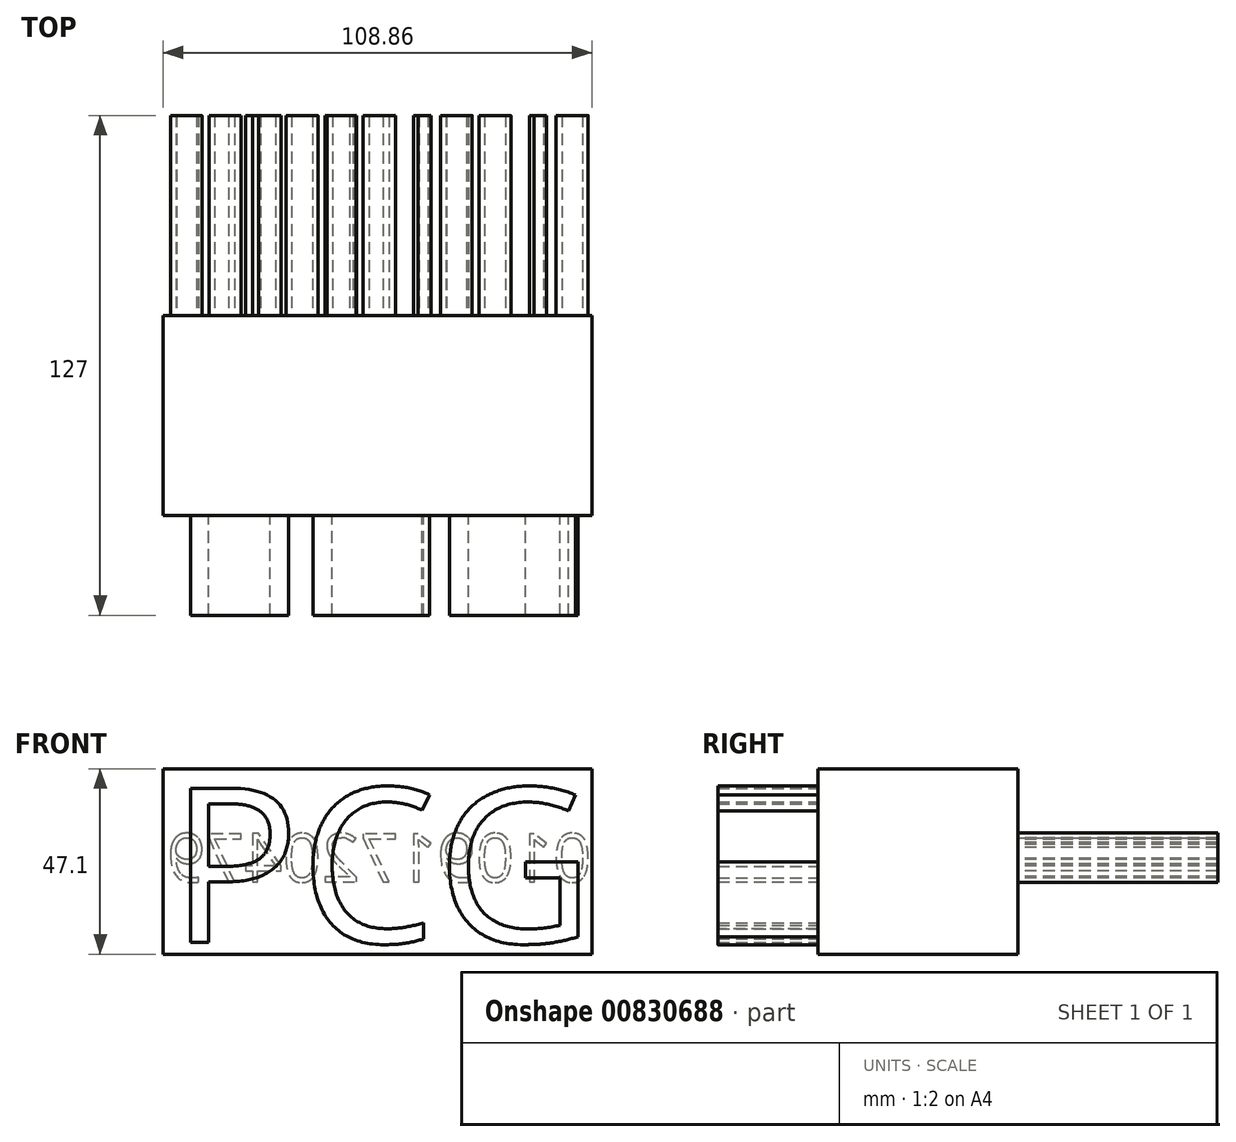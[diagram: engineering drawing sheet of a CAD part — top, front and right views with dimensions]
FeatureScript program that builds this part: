
annotation { "Feature Type Name" : "Feature", "Feature Type Description" : "" }
export const myFeature = defineFeature(function(context is Context, id is Id, definition is map)
    precondition{}
    {
        {
            var Q0;
            Q0=qCreatedBy(makeId("Front.planeOp"),FACE);
            var sketch = newSketch(context, id + "F0", { "sketchPlane" : qUnion([Q0])});
            skLineSegment(sketch, "E0.bottom", {"start": v(0, 0) * mm, "end": v(108.86, 0) * mm});
            skLineSegment(sketch, "E0.top", {"start": v(0, 47.1) * mm, "end": v(108.86, 47.1) * mm});
            skLineSegment(sketch, "E0.left", {"start": v(0, 0) * mm, "end": v(0, 47.1) * mm});
            skLineSegment(sketch, "E0.right", {"start": v(108.86, 0) * mm, "end": v(108.86, 47.1) * mm});
            skSolve(sketch);
        }
        {
            var Q0;
            Q0=makeQuery(id+"F0.imprint","IMPRINT",FACE,{"disambiguationData":[TD([[makeQuery(id+"F0.imprint","IMPRINT",EDGE,{"derivedFrom":sQuery(id+"F0.wireOp",EDGE,"E0.bottom")}),1.0]])]});
            extrude(context, id + "F1", {"entities" : qUnion([Q0]), "depth" : 50.8 * mm, "offsetDistance" : 25.4 * mm});
        }
        {
            var Q0;
            Q0=makeQuery(id+"F1.opExtrude","CAP_FACE",FACE,{"disambiguationData":[OSD([sQuery(id+"F0.wireOp",EDGE,"E0.bottom"),sQuery(id+"F0.wireOp",EDGE,"E0.top"),sQuery(id+"F0.wireOp",EDGE,"E0.left"),sQuery(id+"F0.wireOp",EDGE,"E0.right")])],"isStart":false});
            var sketch = newSketch(context, id + "F2", { "sketchPlane" : qUnion([Q0])});
            skText(sketch, "E1", { "text": "PCG", "fontName": "OpenSans-Regular.ttf"});
            const initialGuessF2  = {"E1": [0.00159, 0.00294, 1, 0, 0.03956]};
            skSetInitialGuess(sketch, initialGuessF2);
            skSolve(sketch);
        }
        {
            var Q0;
            Q0 = qSketchRegion(id + "F2", true);
            extrude(context, id + "F3", {"entities" : qUnion([Q0]), "operationType" : NewBodyOperationType.ADD, "depth" : 25.4 * mm, "offsetDistance" : 25.4 * mm});
        }
        {
            var Q0;
            Q0=makeQuery(id+"F1.opExtrude","CAP_FACE",FACE,{"disambiguationData":[OSD([sQuery(id+"F0.wireOp",EDGE,"E0.bottom"),sQuery(id+"F0.wireOp",EDGE,"E0.top"),sQuery(id+"F0.wireOp",EDGE,"E0.left"),sQuery(id+"F0.wireOp",EDGE,"E0.right")])],"isStart":true});
            var sketch = newSketch(context, id + "F4", { "sketchPlane" : qUnion([Q0])});
            skText(sketch, "E2", { "text": "01091720479", "fontName": "OpenSans-Regular.ttf"});
            const initialGuessF4  = {"E2": [-0.10877, 0.01834, 1, 0, 0.01235]};
            skSetInitialGuess(sketch, initialGuessF4);
            skSolve(sketch);
        }
        {
            var Q0;
            Q0 = qSketchRegion(id + "F4", true);
            extrude(context, id + "F5", {"entities" : qUnion([Q0]), "operationType" : NewBodyOperationType.ADD, "depth" : 50.8 * mm, "offsetDistance" : 25.4 * mm});
        }
    });
